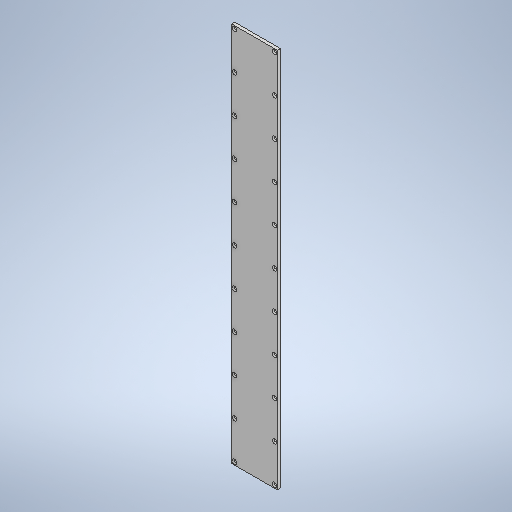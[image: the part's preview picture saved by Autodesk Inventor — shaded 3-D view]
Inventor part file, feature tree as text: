
AUTODESK INVENTOR PART (.ipt)
format: ipt  version: 2025.2 (Build 292293000, 293)  size: 294,912 bytes
history: native  units: mm
features: sketch x2, extrude x1, hole x1, pattern_linear x1
ambient origin geometry x8: Origin, YZ Plane, XZ Plane, XY Plane, X Axis, Y Axis, Z Axis, Center Point
bodies: Volumenkörper1 (feature_tree)
feature tree (5):
  extrude  "Extrusion1"  Depth=60.0mm
  hole  "Bohrung1"  [1 undecoded]
  pattern_linear  "Rechteckige Anordnung1"  Spacing1=3.75mm  [1 undecoded]
  sketch  "Skizze1"  dims[d15=500.0mm d16=60.0mm]
  sketch  "Skizze3"  dims[d17=4.0mm d18=0.0mm d74=4.0mm d75=3.75mm d76=3.0mm d77=6.0mm d78=6.0mm d79=3.0mm d80=90.0deg d81=8.0mm d82=20.594885mm d83=110.0mm d85=49.2mm d86=20.0mm d88=52.5mm]
note: 2 required parameter values undecoded (feature->parameter linkage not recoverable at this tier; creation-order binding heuristic only, values carry confidence <= 0.55)
